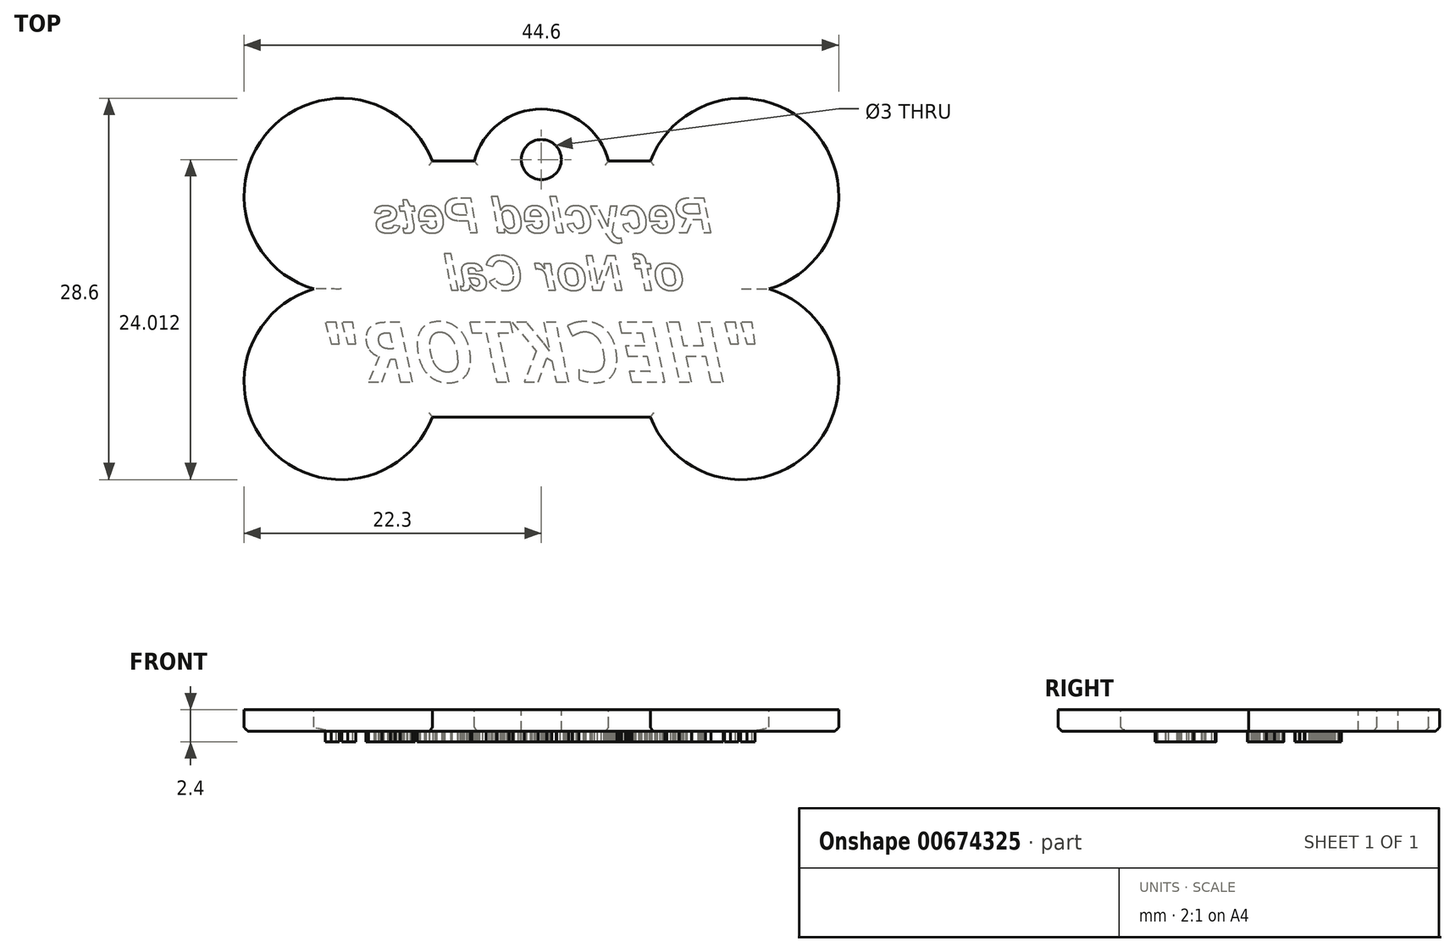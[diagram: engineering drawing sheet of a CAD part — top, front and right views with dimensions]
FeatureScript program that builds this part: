
annotation { "Feature Type Name" : "Feature", "Feature Type Description" : "" }
export const myFeature = defineFeature(function(context is Context, id is Id, definition is map)
    precondition{}
    {
        {
            var Q0;
            Q0=qCreatedBy(makeId("Top.planeOp"),FACE);
            var sketch = newSketch(context, id + "F0", { "sketchPlane" : qUnion([Q0])});
            skLineSegment(sketch, "E0.bottom", {"start": v(15, -7) * mm, "end": v(-15, -7) * mm, "construction": true});
            skLineSegment(sketch, "E0.top", {"start": v(15, 7) * mm, "end": v(-15, 7) * mm, "construction": true});
            skLineSegment(sketch, "E0.left", {"start": v(15, -7) * mm, "end": v(15, 7) * mm, "construction": true});
            skLineSegment(sketch, "E0.right", {"start": v(-15, -7) * mm, "end": v(-15, 7) * mm, "construction": true});
            skPoint(sketch, "E0.middle", {"position": v(0, 0) * mm});
            skArc(sketch, "E1", {"start": v(15, 0.7) * mm, "mid": v(19.99, 10.85) * mm, "end": v(8.9, 8.6) * mm});
            skArc(sketch, "E2", {"start": v(8.9, -8.6) * mm, "mid": v(19.99, -10.85) * mm, "end": v(15, -0.7) * mm});
            skArc(sketch, "E3", {"start": v(-15, -0.7) * mm, "mid": v(-19.99, -10.85) * mm, "end": v(-8.9, -8.6) * mm});
            skArc(sketch, "E4", {"start": v(-8.9, 8.6) * mm, "mid": v(-19.99, 10.85) * mm, "end": v(-15, 0.7) * mm});
            skLineSegment(sketch, "E5", {"start": v(-15, 0.7) * mm, "end": v(-15, -0.7) * mm});
            skLineSegment(sketch, "E6", {"start": v(15, -0.7) * mm, "end": v(15, 0.7) * mm});
            skLineSegment(sketch, "E7", {"start": v(-8.9, 8.6) * mm, "end": v(-4.19, 8.6) * mm});
            skLineSegment(sketch, "E8", {"start": v(-8.9, -8.6) * mm, "end": v(8.9, -8.6) * mm});
            skArc(sketch, "E9", {"start": v(4.19, 8.6) * mm, "mid": v(0, 12.5) * mm, "end": v(-4.19, 8.6) * mm});
            skPoint(sketch, "E10", {"position": v(0, 12.5) * mm});
            skCircle(sketch, "E11", {"center": v(0, 9.71) * mm, "radius": 1.5 * mm});
            skLineSegment(sketch, "E12.trimOffspring", {"start": v(4.19, 8.6) * mm, "end": v(8.9, 8.6) * mm});
            skLineSegment(sketch, "E13.0", {"start": v(-8.18, 9.6) * mm, "end": v(-5.03, 9.6) * mm});
            skArc(sketch, "E13.1", {"start": v(5.03, 9.6) * mm, "mid": v(0, 13.5) * mm, "end": v(-5.03, 9.6) * mm});
            skArc(sketch, "E13.2", {"start": v(-8.18, 9.6) * mm, "mid": v(-20.36, 11.96) * mm, "end": v(-17.07, 0) * mm});
            skLineSegment(sketch, "E13.3", {"start": v(5.03, 9.6) * mm, "end": v(8.18, 9.6) * mm});
            skArc(sketch, "E13.4", {"start": v(-17.07, 0) * mm, "mid": v(-20.36, -11.96) * mm, "end": v(-8.18, -9.6) * mm});
            skLineSegment(sketch, "E13.5", {"start": v(-8.18, -9.6) * mm, "end": v(8.18, -9.6) * mm});
            skArc(sketch, "E13.6", {"start": v(8.18, -9.6) * mm, "mid": v(20.36, -11.96) * mm, "end": v(17.07, 0) * mm});
            skArc(sketch, "E13.7", {"start": v(17.07, 0) * mm, "mid": v(20.36, 11.96) * mm, "end": v(8.18, 9.6) * mm});
            skSolve(sketch);
        }
        {
            var Q0;
            Q0=makeQuery(id+"F0.imprint","IMPRINT",FACE,{"disambiguationData":[TD([[makeQuery(id+"F0.imprint","IMPRINT",EDGE,{"derivedFrom":sQuery(id+"F0.wireOp",EDGE,"E1")}),-1.0]])]});
            extrude(context, id + "F1", {"entities" : qUnion([Q0]), "oppositeDirection" : true, "depth" : .2 * mm, "offsetDistance" : 25 * mm});
        }
        {
            var Q0;
            Q0=makeQuery(id+"F0.imprint","IMPRINT",FACE,{"disambiguationData":[TD([[makeQuery(id+"F0.imprint","IMPRINT",EDGE,{"derivedFrom":sQuery(id+"F0.wireOp",EDGE,"E1")}),1.0]])]});
            var Q1;
            Q1=makeQuery(id+"F0.imprint","IMPRINT",FACE,{"disambiguationData":[TD([[makeQuery(id+"F0.imprint","IMPRINT",EDGE,{"derivedFrom":sQuery(id+"F0.wireOp",EDGE,"E1")}),-1.0]])]});
            extrude(context, id + "F2", {"entities" : qUnion([Q0, Q1]), "operationType" : NewBodyOperationType.ADD, "oppositeDirection" : true, "depth" : 1.6 * mm, "offsetDistance" : 25 * mm});
        }
        {
            var Q0;
            Q0=makeQuery(id+"F2.opExtrude","CAP_FACE",FACE,{"disambiguationData":[OSD([sQuery(id+"F0.wireOp",EDGE,"E11"),sQuery(id+"F0.wireOp",EDGE,"E13.0"),sQuery(id+"F0.wireOp",EDGE,"E13.1"),sQuery(id+"F0.wireOp",EDGE,"E13.2"),sQuery(id+"F0.wireOp",EDGE,"E13.3"),sQuery(id+"F0.wireOp",EDGE,"E13.4"),sQuery(id+"F0.wireOp",EDGE,"E13.5"),sQuery(id+"F0.wireOp",EDGE,"E13.6"),sQuery(id+"F0.wireOp",EDGE,"E13.7")])],"isStart":false});
            var sketch = newSketch(context, id + "F3", { "sketchPlane" : qUnion([Q0])});
            skText(sketch, "E14", { "text": "Recycled Pets \n  of Nor Cal", "fontName": "Arimo-BoldItalic.ttf"});
            skText(sketch, "E15", { "text": "\"HECKTOR\"", "fontName": "OpenSans-BoldItalic.ttf"});
            const initialGuessF3  = {"E14": [0.01278, -0.00423, -1, 0, 0.0027], "E15": [0.01663, 0.00697, -1, 0, 0.0045]};
            skSetInitialGuess(sketch, initialGuessF3);
            skSolve(sketch);
        }
        {
            var Q0;
            Q0=qSketchRegion(id+"F3",true);
            extrude(context, id + "F4", {"entities" : qUnion([Q0]), "operationType" : NewBodyOperationType.ADD, "depth" : .8 * mm, "offsetDistance" : 25 * mm});
        }
        {
            var Q0;
            Q0=makeQuery(id+"F2.opExtrude","CAP_EDGE",EDGE,{"disambiguationData":[OSD([sQuery(id+"F0.wireOp",EDGE,"E13.7")])],"isStart":false});
            var Q1;
            Q1=makeQuery(id+"F2.opExtrude","CAP_EDGE",EDGE,{"disambiguationData":[OSD([sQuery(id+"F0.wireOp",EDGE,"E13.6")])],"isStart":false});
            var Q2;
            Q2=makeQuery(id+"F2.opExtrude","CAP_EDGE",EDGE,{"disambiguationData":[OSD([sQuery(id+"F0.wireOp",EDGE,"E13.3")])],"isStart":false});
            var Q3;
            Q3=makeQuery(id+"F2.opExtrude","CAP_EDGE",EDGE,{"disambiguationData":[OSD([sQuery(id+"F0.wireOp",EDGE,"E13.1")])],"isStart":false});
            var Q4;
            Q4=makeQuery(id+"F2.opExtrude","CAP_EDGE",EDGE,{"disambiguationData":[OSD([sQuery(id+"F0.wireOp",EDGE,"E13.0")])],"isStart":false});
            var Q5;
            Q5=makeQuery(id+"F2.opExtrude","CAP_EDGE",EDGE,{"disambiguationData":[OSD([sQuery(id+"F0.wireOp",EDGE,"E13.2")])],"isStart":false});
            var Q6;
            Q6=makeQuery(id+"F2.opExtrude","CAP_EDGE",EDGE,{"disambiguationData":[OSD([sQuery(id+"F0.wireOp",EDGE,"E13.4")])],"isStart":false});
            var Q7;
            Q7=makeQuery(id+"F2.opExtrude","CAP_EDGE",EDGE,{"disambiguationData":[OSD([sQuery(id+"F0.wireOp",EDGE,"E13.5")])],"isStart":false});
            var Q8;
            Q8=makeQuery(id+"F1.opExtrude","CAP_EDGE",EDGE,{"disambiguationData":[OSD([sQuery(id+"F0.wireOp",EDGE,"E13.5")])],"isStart":false});
            var Q9;
            Q9=makeQuery(id+"F1.opExtrude","CAP_EDGE",EDGE,{"disambiguationData":[OSD([sQuery(id+"F0.wireOp",EDGE,"E13.4")])],"isStart":false});
            var Q10;
            Q10=makeQuery(id+"F1.opExtrude","CAP_EDGE",EDGE,{"disambiguationData":[OSD([sQuery(id+"F0.wireOp",EDGE,"E13.2")])],"isStart":false});
            var Q11;
            Q11=makeQuery(id+"F1.opExtrude","CAP_EDGE",EDGE,{"disambiguationData":[OSD([sQuery(id+"F0.wireOp",EDGE,"E13.0")])],"isStart":false});
            var Q12;
            Q12=makeQuery(id+"F1.opExtrude","CAP_EDGE",EDGE,{"disambiguationData":[OSD([sQuery(id+"F0.wireOp",EDGE,"E13.1")])],"isStart":false});
            var Q13;
            Q13=makeQuery(id+"F1.opExtrude","CAP_EDGE",EDGE,{"disambiguationData":[OSD([sQuery(id+"F0.wireOp",EDGE,"E13.3")])],"isStart":false});
            var Q14;
            Q14=makeQuery(id+"F1.opExtrude","CAP_EDGE",EDGE,{"disambiguationData":[OSD([sQuery(id+"F0.wireOp",EDGE,"E13.7")])],"isStart":false});
            var Q15;
            Q15=makeQuery(id+"F1.opExtrude","CAP_EDGE",EDGE,{"disambiguationData":[OSD([sQuery(id+"F0.wireOp",EDGE,"E13.6")])],"isStart":false});
            fillet(context, id + "F5", {"entities" : qUnion([Q0, Q1, Q2, Q3, Q4, Q5, Q6, Q7, Q8, Q9, Q10, Q11, Q12, Q13, Q14, Q15]), "radius" : .3 * mm, "tangentPropagation" : true, "rho" : .1, "crossSection" : FilletCrossSection.CONIC, "allowEdgeOverflow" : false});
        }
        {
            var Q0;
            Q0=makeQuery(id+"F1.opExtrude","SWEPT_BODY",BODY,{"disambiguationData":[OSD([sQuery(id+"F0.wireOp",EDGE,"E1"),sQuery(id+"F0.wireOp",EDGE,"E2"),sQuery(id+"F0.wireOp",EDGE,"E3"),sQuery(id+"F0.wireOp",EDGE,"E4"),sQuery(id+"F0.wireOp",EDGE,"E5"),sQuery(id+"F0.wireOp",EDGE,"E6"),sQuery(id+"F0.wireOp",EDGE,"E7"),sQuery(id+"F0.wireOp",EDGE,"E8"),sQuery(id+"F0.wireOp",EDGE,"E9"),sQuery(id+"F0.wireOp",EDGE,"E12.trimOffspring"),sQuery(id+"F0.wireOp",EDGE,"E13.0"),sQuery(id+"F0.wireOp",EDGE,"E13.1"),sQuery(id+"F0.wireOp",EDGE,"E13.2"),sQuery(id+"F0.wireOp",EDGE,"E13.3"),sQuery(id+"F0.wireOp",EDGE,"E13.4"),sQuery(id+"F0.wireOp",EDGE,"E13.5"),sQuery(id+"F0.wireOp",EDGE,"E13.6"),sQuery(id+"F0.wireOp",EDGE,"E13.7")])]});
            transform(context, id + "F6", {"entities" : qUnion([Q0]), "transformType" : TransformType.TRANSLATION_3D, "dx" : 0 * mm, "dy" : -41.7 * mm, "dz" : 0 * mm, "makeCopy" : true});
        }
        {
            var Q0;
            Q0=makeQuery(id+"F6.opPattern","COPY",BODY,{"derivedFrom":makeQuery(id+"F1.opExtrude","SWEPT_BODY",BODY,{"disambiguationData":[OSD([sQuery(id+"F0.wireOp",EDGE,"E1"),sQuery(id+"F0.wireOp",EDGE,"E2"),sQuery(id+"F0.wireOp",EDGE,"E3"),sQuery(id+"F0.wireOp",EDGE,"E4"),sQuery(id+"F0.wireOp",EDGE,"E5"),sQuery(id+"F0.wireOp",EDGE,"E6"),sQuery(id+"F0.wireOp",EDGE,"E7"),sQuery(id+"F0.wireOp",EDGE,"E8"),sQuery(id+"F0.wireOp",EDGE,"E9"),sQuery(id+"F0.wireOp",EDGE,"E12.trimOffspring"),sQuery(id+"F0.wireOp",EDGE,"E13.0"),sQuery(id+"F0.wireOp",EDGE,"E13.1"),sQuery(id+"F0.wireOp",EDGE,"E13.2"),sQuery(id+"F0.wireOp",EDGE,"E13.3"),sQuery(id+"F0.wireOp",EDGE,"E13.4"),sQuery(id+"F0.wireOp",EDGE,"E13.5"),sQuery(id+"F0.wireOp",EDGE,"E13.6"),sQuery(id+"F0.wireOp",EDGE,"E13.7")])]}),"instanceName":"1"});
            deleteBodies(context, id + "F7", {"entities" : qUnion([Q0])});
        }
    });
